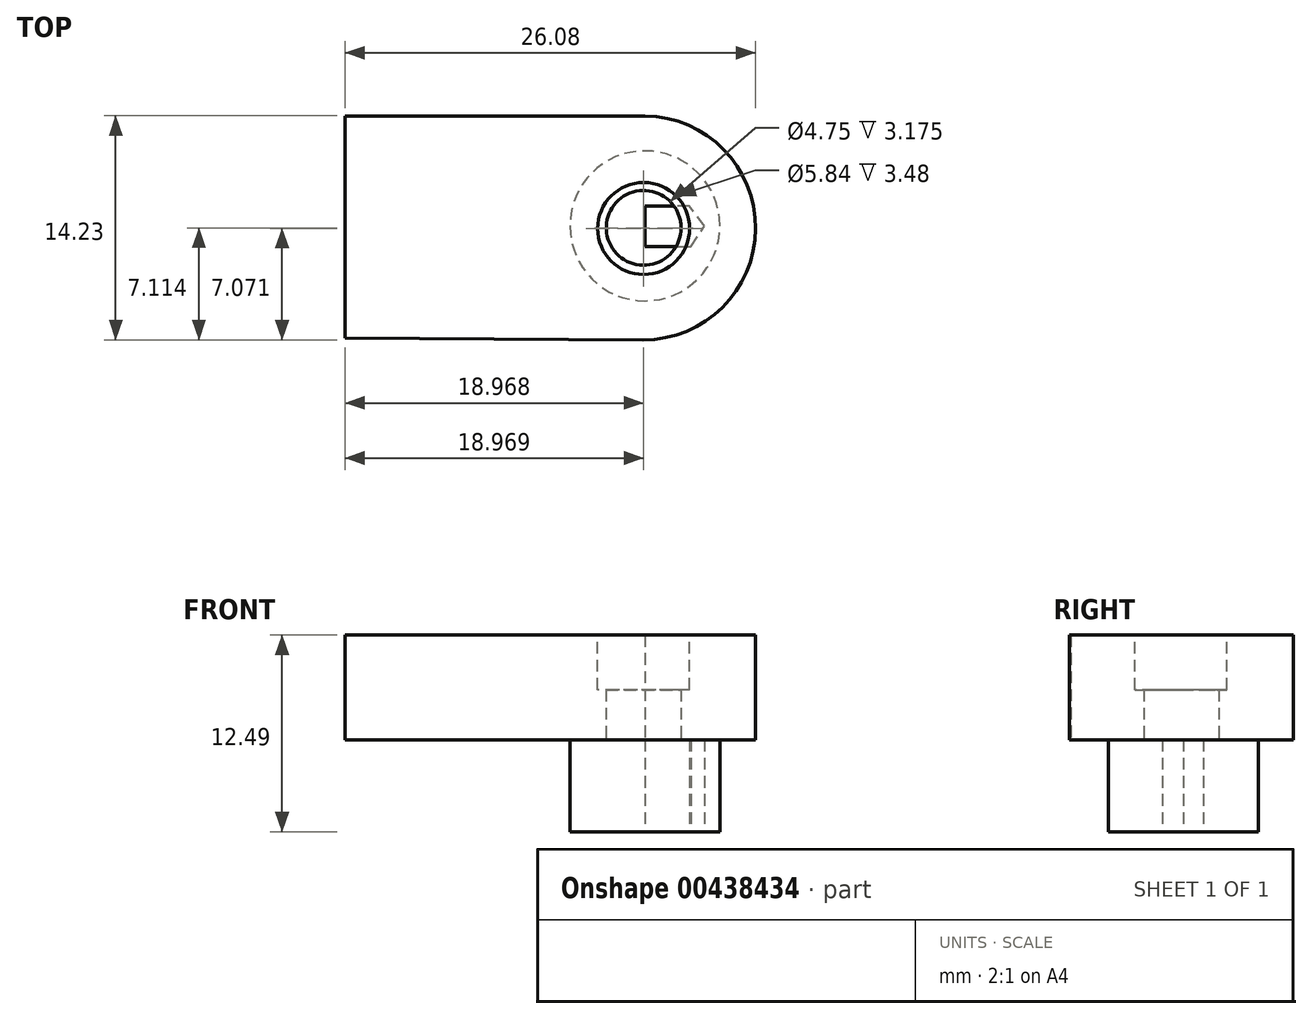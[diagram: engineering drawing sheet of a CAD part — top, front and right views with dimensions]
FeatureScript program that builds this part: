
annotation { "Feature Type Name" : "Feature", "Feature Type Description" : "" }
export const myFeature = defineFeature(function(context is Context, id is Id, definition is map)
    precondition{}
    {
        {
            var Q0;
            Q0=qCreatedBy(makeId("Top.planeOp"),FACE);
            var sketch = newSketch(context, id + "F0", { "sketchPlane" : qUnion([Q0])});
            skLineSegment(sketch, "E0", {"start": v(0, 6.99) * mm, "end": v(-19.05, 6.99) * mm});
            skLineSegment(sketch, "E1", {"start": v(-19.05, 6.99) * mm, "end": v(-19.05, 0) * mm});
            skLineSegment(sketch, "E2", {"start": v(-19.05, 0) * mm, "end": v(-19.05, -7.14) * mm});
            skLineSegment(sketch, "E3", {"start": v(-19.05, -7.14) * mm, "end": v(-0.12, -7.24) * mm});
            skArc(sketch, "E4", {"start": v(-0.12, -7.24) * mm, "mid": v(7.03, -0.19) * mm, "end": v(0, 6.99) * mm});
            skCircle(sketch, "E5", {"center": v(-0.08, -0.13) * mm, "radius": 2.37 * mm});
            skSolve(sketch);
        }
        {
            var Q0;
            Q0 = qSketchRegion(id + "F0", true);
            extrude(context, id + "F1", {"entities" : qUnion([Q0]), "depth" : 6.65 * mm});
        }
        {
            var Q0;
            Q0=qCreatedBy(makeId("Top.planeOp"),FACE);
            var sketch = newSketch(context, id + "F2", { "sketchPlane" : qUnion([Q0])});
            skCircle(sketch, "E6", {"center": v(0, 0) * mm, "radius": 4.76 * mm});
            skSolve(sketch);
        }
        {
            var Q0;
            Q0 = qSketchRegion(id + "F2", true);
            extrude(context, id + "F3", {"entities" : qUnion([Q0]), "operationType" : NewBodyOperationType.ADD, "depth" : -5.84 * mm});
        }
        {
            var Q0;
            Q0=makeQuery(id+"F3.opExtrude","CAP_FACE",FACE,{"disambiguationData":[OSD([sQuery(id+"F2.wireOp",EDGE,"E6")])],"isStart":false});
            var sketch = newSketch(context, id + "F4", { "sketchPlane" : qUnion([Q0])});
            skLineSegment(sketch, "E7", {"start": v(0, 0) * mm, "end": v(0, 1.32) * mm});
            skLineSegment(sketch, "E8", {"start": v(0, 1.32) * mm, "end": v(2.92, 1.32) * mm});
            skLineSegment(sketch, "E9", {"start": v(2.92, 1.32) * mm, "end": v(3.79, 0) * mm});
            skLineSegment(sketch, "E10", {"start": v(3.79, 0) * mm, "end": v(2.83, -1.27) * mm});
            skLineSegment(sketch, "E11", {"start": v(2.83, -1.27) * mm, "end": v(0, -1.27) * mm});
            skLineSegment(sketch, "E12", {"start": v(0, -1.27) * mm, "end": v(0, 0) * mm});
            skSolve(sketch);
        }
        {
            var Q0;
            Q0 = qSketchRegion(id + "F4", true);
            extrude(context, id + "F5", {"entities" : qUnion([Q0]), "operationType" : NewBodyOperationType.REMOVE, "depth" : -5.84 * mm});
        }
        {
            var Q0;
            Q0=qCreatedBy(makeId("Top.planeOp"),FACE);
            cPlane(context, id + "F6", {"entities" : qUnion([Q0]), "cplaneType" : CPlaneType.OFFSET, "offset" : 25.4 * mm, "width" : 152.4 * mm, "height" : 152.4 * mm});
        }
        {
            var Q0;
            Q0=qCreatedBy(id+"F6.planeOp",FACE);
            var sketch = newSketch(context, id + "F7", { "sketchPlane" : qUnion([Q0])});
            skCircle(sketch, "E13", {"center": v(-0.08, -0.17) * mm, "radius": 2.92 * mm});
            skPoint(sketch, "E13.first.point", {"position": v(-2.6, -1.65) * mm});
            skPoint(sketch, "E13.second.point", {"position": v(1.2, 2.45) * mm});
            skPoint(sketch, "E13.third.point", {"position": v(2.84, 0) * mm});
            skSolve(sketch);
        }
        {
            var Q0;
            Q0=makeQuery(id+"F7.imprint","IMPRINT",FACE,{"disambiguationData":[TD([[makeQuery(id+"F7.imprint","IMPRINT",EDGE,{"derivedFrom":sQuery(id+"F7.wireOp",EDGE,"E13")}),1.0]])]});
            extrude(context, id + "F8", {"entities" : qUnion([Q0]), "operationType" : NewBodyOperationType.REMOVE, "oppositeDirection" : true, "depth" : 22.22 * mm});
        }
    });
